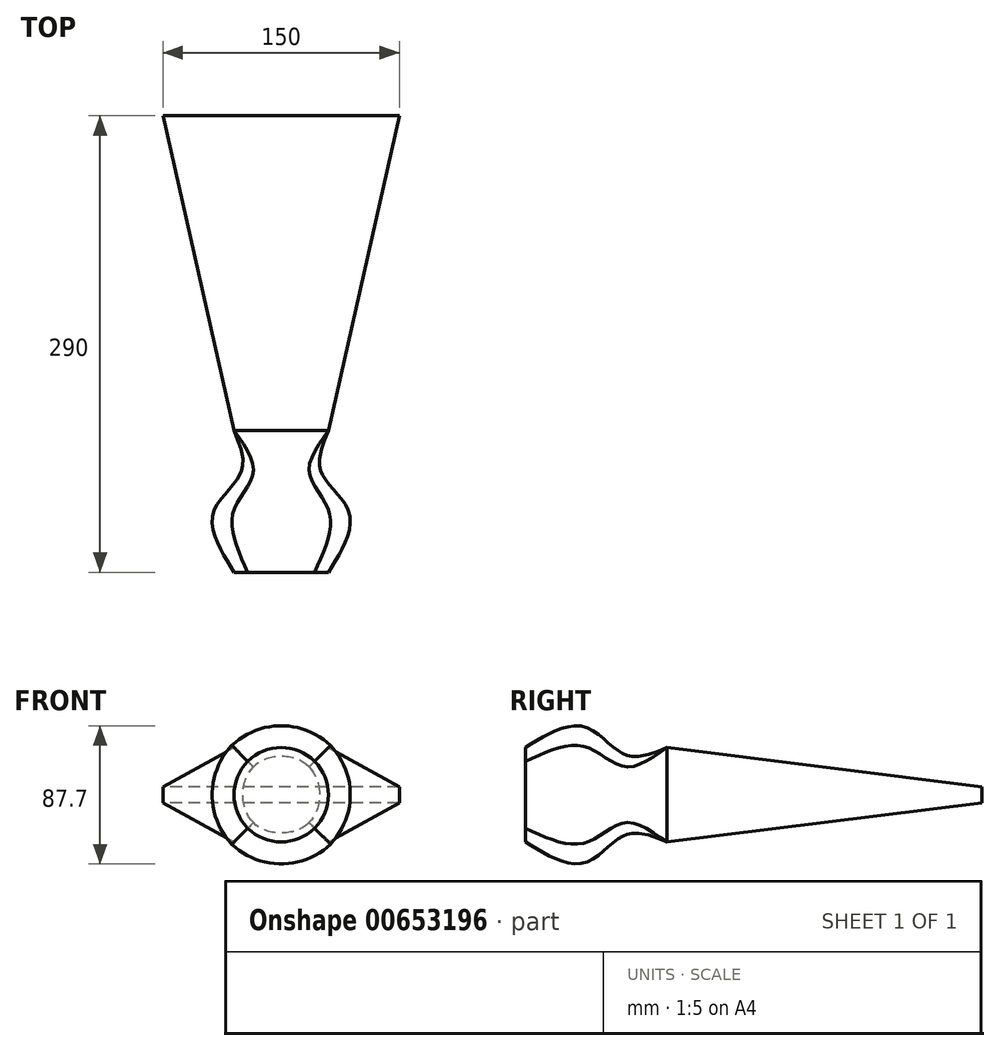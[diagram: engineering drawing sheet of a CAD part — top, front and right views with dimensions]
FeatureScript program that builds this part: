
annotation { "Feature Type Name" : "Feature", "Feature Type Description" : "" }
export const myFeature = defineFeature(function(context is Context, id is Id, definition is map)
    precondition{}
    {
        {
            var Q0;
            Q0=qCreatedBy(makeId("Front.planeOp"),FACE);
            cPlane(context, id + "F0", {"entities" : qUnion([Q0]), "cplaneType" : CPlaneType.OFFSET, "offset" : 25 * mm, "width" : 150 * mm, "height" : 150 * mm});
        }
        {
            var Q0;
            Q0=qCreatedBy(id+"F0.planeOp",FACE);
            cPlane(context, id + "F1", {"entities" : qUnion([Q0]), "cplaneType" : CPlaneType.OFFSET, "offset" : 25 * mm, "width" : 150 * mm, "height" : 150 * mm});
        }
        {
            var Q0;
            Q0=qCreatedBy(id+"F1.planeOp",FACE);
            cPlane(context, id + "F2", {"entities" : qUnion([Q0]), "cplaneType" : CPlaneType.OFFSET, "offset" : 40 * mm, "width" : 150 * mm, "height" : 150 * mm});
        }
        {
            var Q0;
            Q0=qCreatedBy(makeId("Front.planeOp"),FACE);
            var sketch = newSketch(context, id + "F3", { "sketchPlane" : qUnion([Q0])});
            skLineSegment(sketch, "E0.bottom", {"start": v(-30, 30) * mm, "end": v(30, 30) * mm});
            skLineSegment(sketch, "E0.top", {"start": v(-30, -30) * mm, "end": v(30, -30) * mm});
            skLineSegment(sketch, "E0.left", {"start": v(-30, 30) * mm, "end": v(-30, -30) * mm});
            skLineSegment(sketch, "E0.right", {"start": v(30, 30) * mm, "end": v(30, -30) * mm});
            skPoint(sketch, "E0.middle", {"position": v(0, 0) * mm});
            skSolve(sketch);
        }
        {
            var Q0;
            Q0=qCreatedBy(id+"F1.planeOp",FACE);
            var sketch = newSketch(context, id + "F4", { "sketchPlane" : qUnion([Q0])});
            skCircle(sketch, "E1", {"center": v(0, 0) * mm, "radius": 42.35 * mm});
            skSolve(sketch);
        }
        {
            var Q0;
            Q0=qCreatedBy(id+"F2.planeOp",FACE);
            var sketch = newSketch(context, id + "F5", { "sketchPlane" : qUnion([Q0])});
            skCircle(sketch, "E2", {"center": v(0, 0) * mm, "radius": 30 * mm});
            skSolve(sketch);
        }
        {
            var Q0;
            Q0=qCreatedBy(id+"F0.planeOp",FACE);
            var sketch = newSketch(context, id + "F6", { "sketchPlane" : qUnion([Q0])});
            skCircle(sketch, "E3", {"center": v(0, 0) * mm, "radius": 25 * mm});
            skSolve(sketch);
        }
        {
            var Q0;
            Q0 = qSketchRegion(id + "F3", true);
            var Q1;
            Q1=makeQuery(id+"F6.imprint","IMPRINT",FACE,{"disambiguationData":[TD([[makeQuery(id+"F6.imprint","IMPRINT",EDGE,{"derivedFrom":sQuery(id+"F6.wireOp",EDGE,"E3")}),1.0]])]});
            var Q2;
            Q2=makeQuery(id+"F4.imprint","IMPRINT",FACE,{"disambiguationData":[TD([[makeQuery(id+"F4.imprint","IMPRINT",EDGE,{"derivedFrom":sQuery(id+"F4.wireOp",EDGE,"E1")}),1.0]])]});
            var Q3;
            Q3=makeQuery(id+"F5.imprint","IMPRINT",FACE,{"disambiguationData":[TD([[makeQuery(id+"F5.imprint","IMPRINT",EDGE,{"derivedFrom":sQuery(id+"F5.wireOp",EDGE,"E2")}),1.0]])]});
            loft(context, id + "F7", {"sheetProfilesArray" : [{ "sheetProfileEntities" : qUnion([Q0]) }, { "sheetProfileEntities" : qUnion([Q1]) }, { "sheetProfileEntities" : qUnion([Q2]) }, { "sheetProfileEntities" : qUnion([Q3]) }]});
        }
        {
            var Q0;
            Q0=qCreatedBy(makeId("Front.planeOp"),FACE);
            cPlane(context, id + "F8", {"entities" : qUnion([Q0]), "cplaneType" : CPlaneType.OFFSET, "offset" : 200 * mm, "oppositeDirection" : true, "width" : 150 * mm, "height" : 150 * mm});
        }
        {
            var Q0;
            Q0=qCreatedBy(id+"F8.planeOp",FACE);
            var sketch = newSketch(context, id + "F9", { "sketchPlane" : qUnion([Q0])});
            skLineSegment(sketch, "E4.bottom", {"start": v(75, 5) * mm, "end": v(-75, 5) * mm});
            skLineSegment(sketch, "E4.top", {"start": v(75, -5) * mm, "end": v(-75, -5) * mm});
            skLineSegment(sketch, "E4.left", {"start": v(75, 5) * mm, "end": v(75, -5) * mm});
            skLineSegment(sketch, "E4.right", {"start": v(-75, 5) * mm, "end": v(-75, -5) * mm});
            skPoint(sketch, "E4.middle", {"position": v(0, 0) * mm});
            skSolve(sketch);
        }
        {
            var Q1;
            Q1=makeQuery(id+"F7.opLoft","CAP_FACE",FACE,{"disambiguationData":[OSD([makeQuery(id+"F3.imprint","IMPRINT",FACE,{"disambiguationData":[TD([[makeQuery(id+"F3.imprint","IMPRINT",EDGE,{"derivedFrom":sQuery(id+"F3.wireOp",EDGE,"E0.bottom")}),-1.0]])]})])],"isStart":true});
            var Q2;
            Q2=makeQuery(id+"F9.imprint","IMPRINT",FACE,{"disambiguationData":[TD([[makeQuery(id+"F9.imprint","IMPRINT",EDGE,{"derivedFrom":sQuery(id+"F9.wireOp",EDGE,"E4.bottom")}),1.0]])]});
            loft(context, id + "F10", {"operationType" : NewBodyOperationType.ADD, "sheetProfilesArray" : [{ "sheetProfileEntities" : qUnion([Q1]) }, { "sheetProfileEntities" : qUnion([Q2]) }]});
        }
    });
